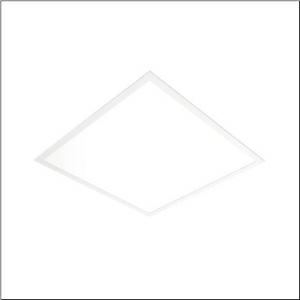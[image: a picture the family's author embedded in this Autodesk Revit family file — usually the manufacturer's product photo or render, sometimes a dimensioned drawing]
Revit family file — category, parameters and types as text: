
# Revit family: apollon_r__41_51mh11wm2m43_8bea
name_source: partatom
category: Lighting Fixtures
units: mm (PartAtom-declared; Revit-internal decimal feet)

## family parameters
Cut with Voids When Loaded = No
Host = Face
Light Source = No
Part Type = Normal
Room Calculation Point = No
Round Connector Dimension = Use Diameter
Shared = No

## types (1)
- --- (1 x LED, 4380 lm, 35 W, 4000K)
    Apparent Load = 35 VA
    CIE Flux Codes = 61 87 97 100 100
    Color Rendering = 80
    Color Temperature = 4000K
    Default Elevation = 1800 mm
    Description = Apollon® 41, office luminaire, primary optical cover: prismatic diffuser, of PS, light emission: direct distribution, primary light characteristic: symmetric, installation type: lay-in mounting, LED, rated luminous flux: 4.375lm, luminous efficacy: 125lm/W, light colour: 830/840, colour temperature: 3000/4000K, control gear: ON/OFF Multilumen, with terminal, 3-pole, mains connection: 220..240V, AC, 50/60Hz, rated input power: 35W, housing, of aluminium section, traffic white (RAL 9016), module: M625, length: 620mm, width: 620mm, height: 60mm, recess depth: 180mm, housing upper side, of sheet steel, protection rating (complete): IP20, protection rating (lamp compartment, on room side): IP40, insulation class (complete): insulation class II (safety insulation), certification: CE, ENEC, impact resistance: IK03, permissible operating ambient temperature: -25..+40°C, packaging unit: 1 piece
    Height = 0 mm  [stored 0 ft]
    Lamp = 1 x LED
    Lamp Light Flux = 4380 lm
    Lamp Power = 35 W
    Lamp count = 1
    Length = 620 mm
    Luminous efficacy = 125 lm/W
    Manufacturer = Siteco
    ModVariant = No
    Model = 51MH11WM2M43
    Mounting Place = Ceiling
    Mounting Type = Recessed
    Number of Poles = 1
    OnlyDefault = Yes
    Power Factor = 1
    Product Name = Apollon® 41
    Product group = office luminaire | ceiling recessed
    ProductGroupID = 401
    Protection Class = Protection class II
    Protection Degree = IP 20
    RLX_Detail_Level = 1
    RLX_Emergency_Light_Flux = 0 lm
    RLX_Emergency_Type = 0
    RLX_Emergency_Type_DB = No
    RlxData = <blob elided: 13585 chars, md5=eeb2fe84>
    Socket = socket
    Standby Power = 0 W
    System Light Flux = 4380 lm
    System Power = 35 W
    Type Comments = factory setting: luminous flux: 100 % | (ON | ON) | 900 mA
    Type Image = l_1291024.jpg
    URL = http://relux.com
    VarID = @adj_013639
    Voltage = 0 V
    Weight = 0.00 kg
    Width = 620 mm

note: [stored X ft] marks values corroborated as IEEE doubles in the binary element streams (Revit-internal decimal feet)

## geometry (parser evidence)
native form markers: Sweep x12
no freeform markers — native parametric forms only
